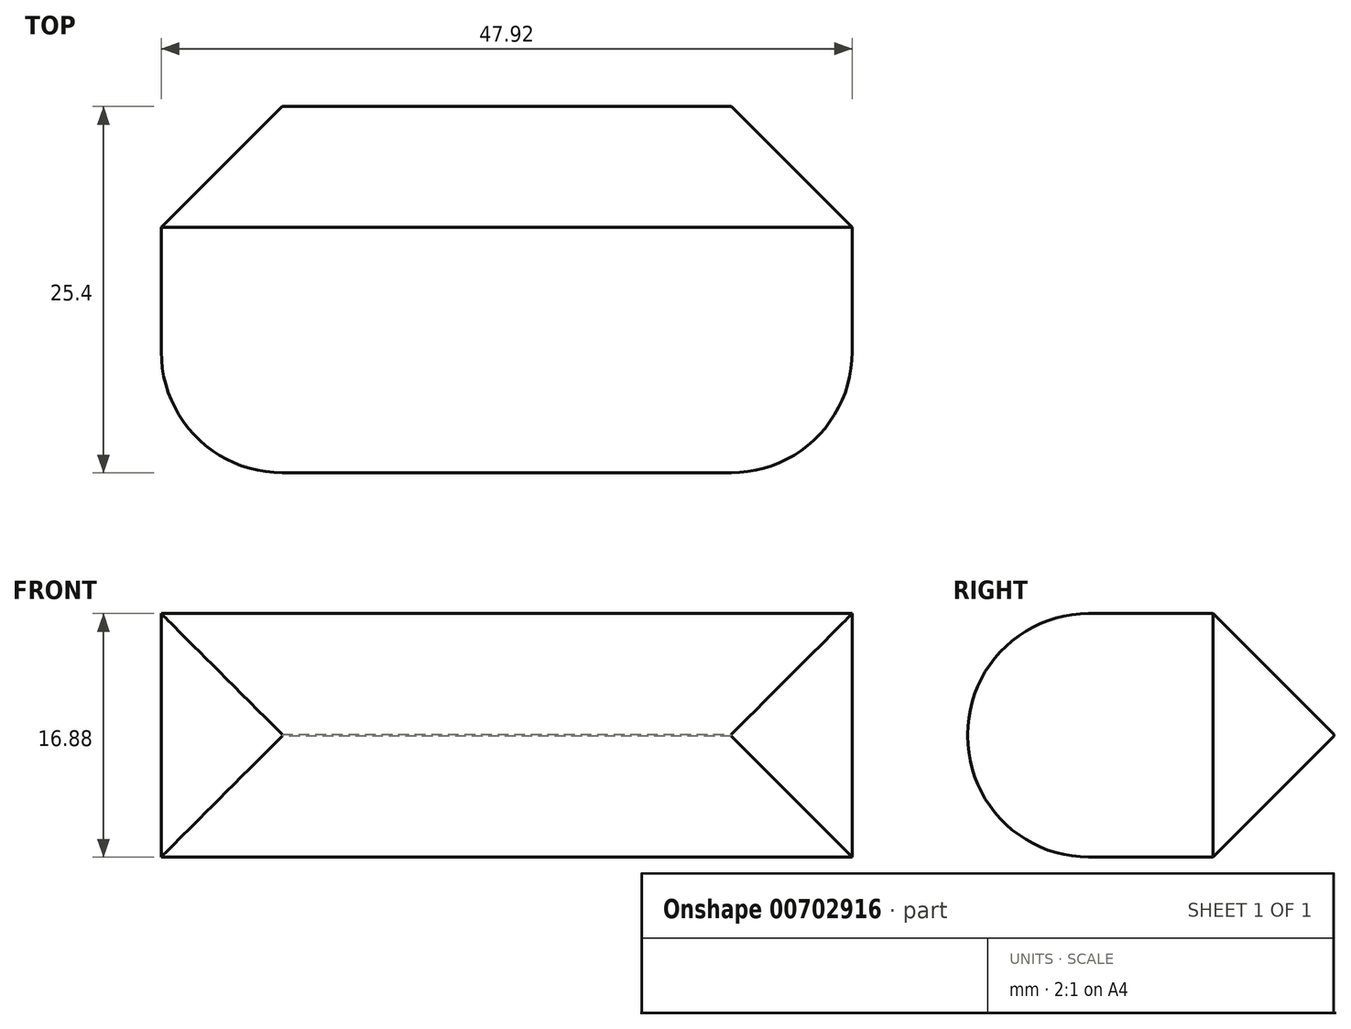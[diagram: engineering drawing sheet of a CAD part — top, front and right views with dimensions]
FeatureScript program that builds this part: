
annotation { "Feature Type Name" : "Feature", "Feature Type Description" : "" }
export const myFeature = defineFeature(function(context is Context, id is Id, definition is map)
    precondition{}
    {
        {
            var Q0;
            Q0=qCreatedBy(makeId("Front.planeOp"),FACE);
            var sketch = newSketch(context, id + "F0", { "sketchPlane" : qUnion([Q0])});
            skLineSegment(sketch, "E0.bottom", {"start": v(-23.96, 8.44) * mm, "end": v(23.96, 8.44) * mm});
            skLineSegment(sketch, "E0.top", {"start": v(-23.96, -8.44) * mm, "end": v(23.96, -8.44) * mm});
            skPoint(sketch, "E0.middle", {"position": v(0, 0) * mm});
            skLineSegment(sketch, "E1", {"start": v(-23.96, -8.44) * mm, "end": v(-23.96, 8.44) * mm});
            skLineSegment(sketch, "E2", {"start": v(23.96, 8.44) * mm, "end": v(23.96, -8.44) * mm});
            skSolve(sketch);
        }
        {
            var Q0;
            Q0 = qSketchRegion(id + "F0", true);
            extrude(context, id + "F1", {"entities" : qUnion([Q0]), "endBound" : BoundingType.SYMMETRIC, "depth" : 25.4 * mm, "offsetDistance" : 25.4 * mm});
        }
        {
            var Q0;
            Q0=makeQuery(id+"F1.opExtrude","CAP_EDGE",EDGE,{"disambiguationData":[OSD([sQuery(id+"F0.wireOp",EDGE,"E0.bottom")])],"isStart":false});
            var Q1;
            Q1=makeQuery(id+"F1.opExtrude","CAP_EDGE",EDGE,{"disambiguationData":[OSD([sQuery(id+"F0.wireOp",EDGE,"bPjhamW6-RC2W-9JE1-0YHi-2cumGAXakoaU")])],"isStart":false});
            var Q2;
            Q2=makeQuery(id+"F1.opExtrude","CAP_EDGE",EDGE,{"disambiguationData":[OSD([sQuery(id+"F0.wireOp",EDGE,"E0.top")])],"isStart":false});
            var Q3;
            Q3=makeQuery(id+"F1.opExtrude","CAP_EDGE",EDGE,{"disambiguationData":[OSD([sQuery(id+"F0.wireOp",EDGE,"BypbZqwH-C0Xc-o4EG-zHvT-Kut19Wl05AoM")])],"isStart":false});
            var Q4;
            Q4=makeQuery(id+"F1.opExtrude","CAP_EDGE",EDGE,{"disambiguationData":[OSD([sQuery(id+"F0.wireOp",EDGE,"E1")])],"isStart":false});
            var Q5;
            Q5=makeQuery(id+"F1.opExtrude","CAP_EDGE",EDGE,{"disambiguationData":[OSD([sQuery(id+"F0.wireOp",EDGE,"E2")])],"isStart":false});
            fillet(context, id + "F2", {"entities" : qUnion([Q0, Q1, Q2, Q3, Q4, Q5]), "radius" : 8.38 * mm, "tangentPropagation" : true, "allowEdgeOverflow" : false});
        }
        {
            var Q0;
            Q0=makeQuery(id+"F1.opExtrude","CAP_EDGE",EDGE,{"disambiguationData":[OSD([sQuery(id+"F0.wireOp",EDGE,"E0.bottom")])],"isStart":true});
            var Q1;
            Q1=makeQuery(id+"F1.opExtrude","CAP_EDGE",EDGE,{"disambiguationData":[OSD([sQuery(id+"F0.wireOp",EDGE,"E2")])],"isStart":true});
            var Q2;
            Q2=makeQuery(id+"F1.opExtrude","CAP_EDGE",EDGE,{"disambiguationData":[OSD([sQuery(id+"F0.wireOp",EDGE,"E0.top")])],"isStart":true});
            var Q3;
            Q3=makeQuery(id+"F1.opExtrude","CAP_EDGE",EDGE,{"disambiguationData":[OSD([sQuery(id+"F0.wireOp",EDGE,"E1")])],"isStart":true});
            chamfer(context, id + "F3", {"entities" : qUnion([Q0, Q1, Q2, Q3]), "width" : 8.38 * mm, "tangentPropagation" : true});
        }
    });
